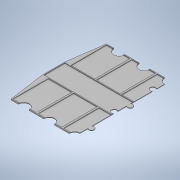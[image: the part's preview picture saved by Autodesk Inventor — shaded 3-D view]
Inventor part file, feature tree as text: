
AUTODESK INVENTOR PART (.ipt)
format: ipt  version: 2021 (Build 250183000, 183)  size: 354,816 bytes
history: native  units: mm
features: extrude x5, projected_geometry x3, sketch x2, pattern_circular x1
ambient origin geometry x8: Origin, YZ Plane, XZ Plane, XY Plane, X Axis, Y Axis, Z Axis, Center Point
bodies: Solid1 (feature_tree)
feature tree (11):
  sketch  "Sketch1"  dims[d0=252.0mm d1=39.0mm]
  extrude  "Extrusion1"  Depth=39.0mm
  extrude  "Extrusion2"  Depth=1.6mm
  extrude  "Extrusion3"  Depth=4.75mm
  extrude  "Extrusion4"  Depth=4.75mm
  pattern_circular  "Circular Pattern1"  [2 undecoded]
  extrude  "Extrusion5"  Depth=47.2mm
  sketch  "Sketch2"  dims[d2=1.6mm d3=1.6mm d5=42.0mm d6=64.0mm d7=1.0mm d8=50.0mm d10=47.2mm d11=10.0mm d13=10.0mm d15=1.0mm d16=3.2mm d17=1.6mm d18=1.6mm d19=10.0mm d20=1.0mm d21=0.0mm d22=1.0mm d23=0.0mm d24=1.0mm d25=0.0mm d26=1.0mm d27=0.0mm d28=20.0mm d29=360.0deg d31=12.0mm d32=12.0mm d33=5.0mm d34=4.75mm d35=3.0mm d36=3.0mm d39=0.0mm d40=0.0mm d41=60.0mm d42=60.0mm d43=5.0mm d44=4.75mm]
  projected_geometry  "Projected Loop1"
  projected_geometry  "Projected Loop2"
  projected_geometry  "Projected Loop3"
note: 2 required parameter values undecoded (feature->parameter linkage not recoverable at this tier; creation-order binding heuristic only, values carry confidence <= 0.55)
